# Revit family: 3f_filippi_-_3f_emilio_track_spot_3f_filippi_-_47559_-_3f_emilio_tk_led_3000-827
name_source: partatom
category: Lighting Fixtures
units: mm (PartAtom-declared; Revit-internal decimal feet)

## family parameters
Cut with Voids When Loaded = No
Host = Face
Light Source = No
Part Type = Normal
Room Calculation Point = No
Round Connector Dimension = Use Diameter
Shared = No

## types (1)
- 3F Filippi - 3F Emilio Track Spot (1 x LED, 3142 lm, 34 W, 2700 K)
    Apparent Load = 34 VA
    Approval mark = CE
    CIE Flux Codes = 84 94 99 100 100
    Color Rendering = 80
    Color Temperature = 2700 K
    Control Gear = Electronic ballast
    Default Elevation = 1800 mm
    Description = Adjustable spot light with minimal dimensions for accent lighting, to be integrated into the busbar.

ILLUMINOTECHNICAL
Luminous efficiency 100% (DLOR 100%, ULOR 0%).
Initial luminous flux of the luminaire 3142 lm.
Symmetrical spot distribution.
Tabular UGR (CIE 117 - 4H-8H; S=0.25H; 70/50/20): RUG 23.7 - 23.7.
Beam angle: 28° - 32°.
Luminous efficacy 92 lm/W.
Lifetime (L90/B20): 30000 h. (tq+25°C)
Lifetime (L80/B20): 50000 h. (tq+25°C)
Sudden decreased luminous flux after 50000 hours: 0% (C0).
Photobiological safety in compliance with IEC/TR 62778: RG1 low risk, (IEC 62471).
In compliance with IEC/EN 62722-2-1 - IEC/EN 62717 standards.

SOURCE
Compact LED module 3000/827.
Energy efficiency class (UE 2019/2020 - UE 2019/2015): E.
CIE 13.3 Colour rendering index: CRI >80 (R9 <50%).
IES TM-30 Fidelity Index: Rf = 84 Rg = 95.
CCT nominal colour temperature 2700 K.
Colour initial tolerance (MacAdam): SDCM 3.
Zhaga Book 3 compliant.

MECHANICAL
Wired unit in white polycarbonate with busbar adaptor.
Single-piece in die-cast aluminium with passive dissipation, white colour, with perimeter cooling slots on upper edge, giving a crown of light effect to the fitting.
Invisible lock for positioning the luminous flux.
Lens made from transparent methacrylate (PMMA) with glossy surface and differentiated photo-etched.
Positioning arm in galvanised brass with sphere to allow for vertical positioning at angles from 0° to 90° and horizontal positioning from 0° to 290°.
Dimensions: diameter 130 mm, length 230 mm, height 105 mm. Weight 0.805 kg.
IP20 protection degree.
Glow-wire test resistance 650°C.

ELECTRICAL
Wiring unit separate from the body, invisible and integrated into the busbar.
Halogen Free electronic wiring 230V-50/60Hz, power factor 0.95, THD <25%, constant output current, SELV, class II, 1 driver.
Power of the luminaire 34 W.
ENEC - CE.
SAFE FLICKER: PstLM=<1 and SVM=<0.4 (IEC TR 61547-1 and IEC TR 63158), to ensure a more comfortable and safe light.
Ambient temperature from 0°C to +25°C.
Temperature class T6 max 85°C.
Relative humidity UR: <85%.

INSTALLATION
Track.

APPLICATIONS
Transit areas, spotlighting in commercial environments, exhibition areas, restaurants, shops and shop windows.

WARNING
Luminaire designed for disposal/recycling at end-of-life.
Replaceable (LED only) light source by a professional. Replaceable control gear by a professional.
    Height = 105 mm
    Lamp = 1 x LED
    Lamp Light Flux = 3142 lm
    Lamp Power = 34 W
    Lamp count = 1
    Length = 230 mm
    Lifetime = 50000 h
    Luminous efficacy = 92 lm/W
    Manufacturer = 3F Filippi
    ModVariant = No
    Model = 3F Filippi - 47559 - 3F Emilio TK LED 3000-827
    Mounting Place = Ceiling
    Mounting Type = Rail mounted
    Number of Poles = 1
    OnlyDefault = Yes
    Power Factor = 1
    Product Name = 3F Filippi - 3F Emilio Track Spot
    Product group = track mounted spotlight
    ProductGroupID = 12
    Protection Class = Protection class II
    Protection Degree = IP 20
    RLX_Detail_Level = 1
    RLX_Emergency_Light_Flux = 0 lm
    RLX_Emergency_Type = 0
    RLX_Emergency_Type_DB = No
    RlxData = <blob elided: 149689 chars, md5=a5460f52>
    Socket = socket
    Standby Power = 0 W
    System Light Flux = 3142 lm
    System Power = 34 W
    Type Comments = Product without accessories
    Type Image = 3ffilippi_47559.jpg
    URL = http://relux.com
    VarID = ---
    Voltage = 0 V
    Weight = 0.00 kg
    Width = 130 mm

## geometry (parser evidence)
native form markers: Sweep x17
no freeform markers — native parametric forms only
